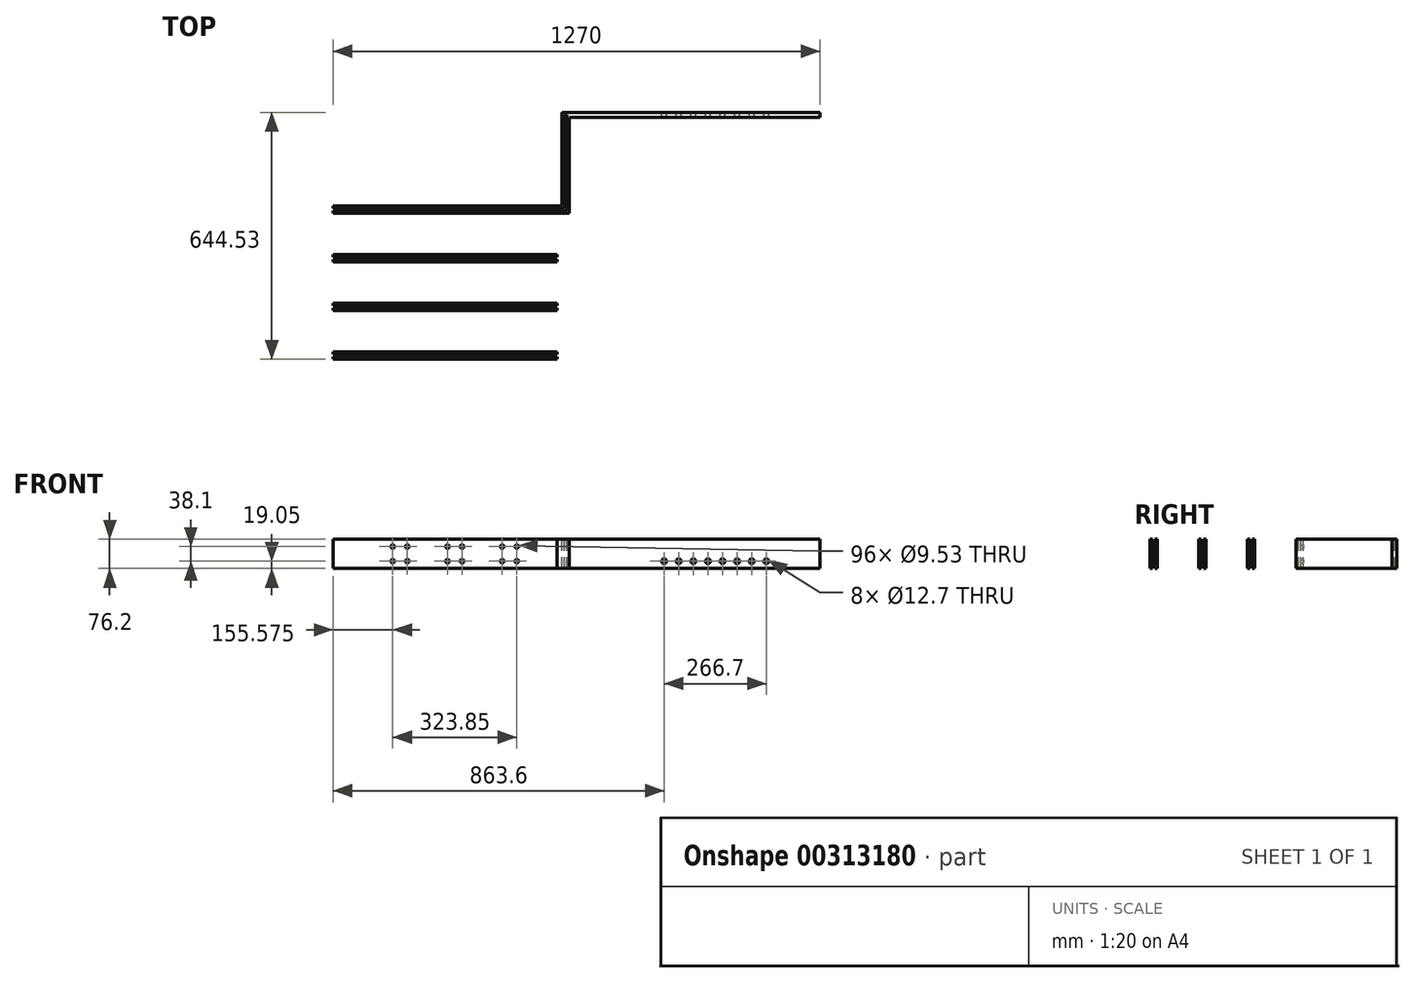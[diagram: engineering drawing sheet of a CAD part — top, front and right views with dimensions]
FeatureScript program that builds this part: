
annotation { "Feature Type Name" : "Feature", "Feature Type Description" : "" }
export const myFeature = defineFeature(function(context is Context, id is Id, definition is map)
    precondition{}
    {
        {
            var Q0;
            Q0=qCreatedBy(makeId("Right.planeOp"),FACE);
            var sketch = newSketch(context, id + "F0", { "sketchPlane" : qUnion([Q0])});
            skLineSegment(sketch, "E0.bottom", {"start": v(0, 0) * mm, "end": v(6.35, 0) * mm});
            skLineSegment(sketch, "E0.top", {"start": v(0, 76.2) * mm, "end": v(6.35, 76.2) * mm});
            skLineSegment(sketch, "E0.left", {"start": v(0, 0) * mm, "end": v(0, 76.2) * mm});
            skLineSegment(sketch, "E0.right", {"start": v(6.35, 0) * mm, "end": v(6.35, 76.2) * mm});
            skLineSegment(sketch, "E1.bottom", {"start": v(12.7, 0) * mm, "end": v(19.05, 0) * mm});
            skLineSegment(sketch, "E1.top", {"start": v(12.7, 76.2) * mm, "end": v(19.05, 76.2) * mm});
            skLineSegment(sketch, "E1.left", {"start": v(12.7, 0) * mm, "end": v(12.7, 76.2) * mm});
            skLineSegment(sketch, "E1.right", {"start": v(19.05, 0) * mm, "end": v(19.05, 76.2) * mm});
            skLineSegment(sketch, "E2.1.0.0", {"start": v(133.35, 0) * mm, "end": v(133.35, 76.2) * mm});
            skLineSegment(sketch, "E2.1.0.1", {"start": v(127, 0) * mm, "end": v(127, 76.2) * mm});
            skLineSegment(sketch, "E2.1.0.2", {"start": v(127, 76.2) * mm, "end": v(133.35, 76.2) * mm});
            skLineSegment(sketch, "E2.1.0.3", {"start": v(127, 0) * mm, "end": v(133.35, 0) * mm});
            skLineSegment(sketch, "E2.1.0.4", {"start": v(139.7, 0) * mm, "end": v(139.7, 76.2) * mm});
            skLineSegment(sketch, "E2.1.0.5", {"start": v(146.05, 0) * mm, "end": v(146.05, 76.2) * mm});
            skLineSegment(sketch, "E2.1.0.6", {"start": v(139.7, 76.2) * mm, "end": v(146.05, 76.2) * mm});
            skLineSegment(sketch, "E2.1.0.7", {"start": v(139.7, 0) * mm, "end": v(146.05, 0) * mm});
            skLineSegment(sketch, "E2.2.0.0", {"start": v(260.35, 0) * mm, "end": v(260.35, 76.2) * mm});
            skLineSegment(sketch, "E2.2.0.1", {"start": v(254, 0) * mm, "end": v(254, 76.2) * mm});
            skLineSegment(sketch, "E2.2.0.2", {"start": v(254, 76.2) * mm, "end": v(260.35, 76.2) * mm});
            skLineSegment(sketch, "E2.2.0.3", {"start": v(254, 0) * mm, "end": v(260.35, 0) * mm});
            skLineSegment(sketch, "E2.2.0.4", {"start": v(266.7, 0) * mm, "end": v(266.7, 76.2) * mm});
            skLineSegment(sketch, "E2.2.0.5", {"start": v(273.05, 0) * mm, "end": v(273.05, 76.2) * mm});
            skLineSegment(sketch, "E2.2.0.6", {"start": v(266.7, 76.2) * mm, "end": v(273.05, 76.2) * mm});
            skLineSegment(sketch, "E2.2.0.7", {"start": v(266.7, 0) * mm, "end": v(273.05, 0) * mm});
            skLineSegment(sketch, "E2.3.0.0", {"start": v(387.35, 0) * mm, "end": v(387.35, 76.2) * mm});
            skLineSegment(sketch, "E2.3.0.1", {"start": v(381, 0) * mm, "end": v(381, 76.2) * mm});
            skLineSegment(sketch, "E2.3.0.2", {"start": v(381, 76.2) * mm, "end": v(387.35, 76.2) * mm});
            skLineSegment(sketch, "E2.3.0.3", {"start": v(381, 0) * mm, "end": v(387.35, 0) * mm});
            skLineSegment(sketch, "E2.3.0.4", {"start": v(393.7, 0) * mm, "end": v(393.7, 76.2) * mm});
            skLineSegment(sketch, "E2.3.0.5", {"start": v(400.05, 0) * mm, "end": v(400.05, 76.2) * mm});
            skLineSegment(sketch, "E2.3.0.6", {"start": v(393.7, 76.2) * mm, "end": v(400.05, 76.2) * mm});
            skLineSegment(sketch, "E2.3.0.7", {"start": v(393.7, 0) * mm, "end": v(400.05, 0) * mm});
            skLineSegment(sketch, "E2.direction1", {"start": v(0, 0) * mm, "end": v(127, 0) * mm, "construction": true});
            skSolve(sketch);
        }
        {
            var Q0;
            Q0 = qSketchRegion(id + "F0", true);
            extrude(context, id + "F1", {"entities" : qUnion([Q0]), "depth" : 584.2 * mm});
        }
        {
            var Q0;
            Q0=makeQuery(id+"F1.opExtrude","SWEPT_FACE",FACE,{"disambiguationData":[OSD([sQuery(id+"F0.wireOp",EDGE,"E2.3.0.6")])]});
            var sketch = newSketch(context, id + "F2", { "sketchPlane" : qUnion([Q0])});
            skLineSegment(sketch, "E3", {"start": v(584.2, 393.7) * mm, "end": v(584.2, 400.05) * mm});
            skLineSegment(sketch, "E4", {"start": v(584.2, 400.05) * mm, "end": v(596.9, 400.05) * mm});
            skLineSegment(sketch, "E5", {"start": v(596.9, 400.05) * mm, "end": v(596.9, 644.53) * mm});
            skLineSegment(sketch, "E6", {"start": v(596.9, 644.53) * mm, "end": v(1270, 644.53) * mm});
            skLineSegment(sketch, "E7", {"start": v(1270, 644.53) * mm, "end": v(1270, 638.18) * mm});
            skLineSegment(sketch, "E8", {"start": v(1270, 638.18) * mm, "end": v(603.25, 638.18) * mm});
            skLineSegment(sketch, "E9", {"start": v(603.25, 638.18) * mm, "end": v(603.25, 393.7) * mm});
            skLineSegment(sketch, "E10", {"start": v(603.25, 393.7) * mm, "end": v(584.2, 393.7) * mm});
            skSolve(sketch);
        }
        {
            var Q0;
            Q0 = qSketchRegion(id + "F2", true);
            extrude(context, id + "F3", {"entities" : qUnion([Q0]), "operationType" : NewBodyOperationType.ADD, "oppositeDirection" : true, "depth" : 76.2 * mm});
        }
        {
            var Q0;
            Q0=makeQuery(id+"F1.opExtrude","SWEPT_FACE",FACE,{"disambiguationData":[OSD([sQuery(id+"F0.wireOp",EDGE,"E2.3.0.2")])]});
            var sketch = newSketch(context, id + "F4", { "sketchPlane" : qUnion([Q0])});
            skLineSegment(sketch, "E11", {"start": v(584.2, 387.35) * mm, "end": v(609.6, 387.35) * mm});
            skLineSegment(sketch, "E12", {"start": v(609.6, 387.35) * mm, "end": v(609.6, 638.18) * mm});
            skLineSegment(sketch, "E13", {"start": v(609.6, 638.18) * mm, "end": v(1270, 638.18) * mm});
            skLineSegment(sketch, "E14", {"start": v(1270, 638.18) * mm, "end": v(1270, 631.83) * mm});
            skLineSegment(sketch, "E15", {"start": v(1270, 631.83) * mm, "end": v(615.95, 631.82) * mm});
            skLineSegment(sketch, "E16", {"start": v(615.95, 631.82) * mm, "end": v(615.95, 381) * mm});
            skLineSegment(sketch, "E17", {"start": v(615.95, 381) * mm, "end": v(584.2, 381) * mm});
            skLineSegment(sketch, "E18", {"start": v(584.2, 381) * mm, "end": v(584.2, 387.35) * mm});
            skSolve(sketch);
        }
        {
            var Q0;
            Q0 = qSketchRegion(id + "F4", true);
            extrude(context, id + "F5", {"entities" : qUnion([Q0]), "operationType" : NewBodyOperationType.ADD, "oppositeDirection" : true, "depth" : 76.2 * mm});
        }
        {
            var Q0;
            Q0=makeQuery(id+"F3.opExtrude","SWEPT_FACE",FACE,{"disambiguationData":[OSD([sQuery(id+"F2.wireOp",EDGE,"E6")])]});
            var sketch = newSketch(context, id + "F6", { "sketchPlane" : qUnion([Q0])});
            skCircle(sketch, "E19", {"center": v(-1130.3, 19.05) * mm, "radius": 6.35 * mm});
            skCircle(sketch, "E20.1.0.0", {"center": v(-1092.2, 19.05) * mm, "radius": 6.35 * mm});
            skCircle(sketch, "E20.2.0.0", {"center": v(-1054.1, 19.05) * mm, "radius": 6.35 * mm});
            skCircle(sketch, "E20.3.0.0", {"center": v(-1016, 19.05) * mm, "radius": 6.35 * mm});
            skLineSegment(sketch, "E20.direction1", {"start": v(-1130.3, 19.05) * mm, "end": v(-1092.2, 19.05) * mm, "construction": true});
            skCircle(sketch, "E21.0.4.0", {"center": v(-977.9, 19.05) * mm, "radius": 6.35 * mm});
            skCircle(sketch, "E21.0.5.0", {"center": v(-939.8, 19.05) * mm, "radius": 6.35 * mm});
            skCircle(sketch, "E21.0.6.0", {"center": v(-901.7, 19.05) * mm, "radius": 6.35 * mm});
            skCircle(sketch, "E21.0.7.0", {"center": v(-863.6, 19.05) * mm, "radius": 6.35 * mm});
            skLineSegment(sketch, "E22", {"start": v(-1130.3, 19.05) * mm, "end": v(-863.6, 19.05) * mm, "construction": true});
            skPoint(sketch, "E23", {"position": v(-996.95, 19.05) * mm});
            skSolve(sketch);
        }
        {
            var Q0;
            Q0 = qSketchRegion(id + "F6", true);
            extrude(context, id + "F7", {"entities" : qUnion([Q0]), "operationType" : NewBodyOperationType.REMOVE, "endBound" : BoundingType.THROUGH_ALL, "oppositeDirection" : true, "depth" : 25.4 * mm});
        }
        {
            var Q0;
            Q0=makeQuery(id+"F3.boolean.opBoolean","MERGE",FACE,{"derivedFrom":[makeQuery(id+"F1.opExtrude","SWEPT_FACE",FACE,{"disambiguationData":[OSD([sQuery(id+"F0.wireOp",EDGE,"E2.3.0.5")])]}),makeQuery(id+"F3.opExtrude","SWEPT_FACE",FACE,{"disambiguationData":[OSD([sQuery(id+"F2.wireOp",EDGE,"E4")])]})]});
            var sketch = newSketch(context, id + "F8", { "sketchPlane" : qUnion([Q0])});
            skLineSegment(sketch, "E24.bottom", {"start": v(-298.45, 57.15) * mm, "end": v(-336.55, 57.15) * mm, "construction": true});
            skLineSegment(sketch, "E24.top", {"start": v(-298.45, 19.05) * mm, "end": v(-336.55, 19.05) * mm, "construction": true});
            skLineSegment(sketch, "E24.left", {"start": v(-298.45, 57.15) * mm, "end": v(-298.45, 19.05) * mm, "construction": true});
            skLineSegment(sketch, "E24.right", {"start": v(-336.55, 57.15) * mm, "end": v(-336.55, 19.05) * mm, "construction": true});
            skPoint(sketch, "E24.middle", {"position": v(-317.5, 38.1) * mm});
            skPoint(sketch, "E24.middle.positionSnap0", {"position": v(0, 38.1) * mm});
            skPoint(sketch, "E24.centerSnap0", {"position": v(0, 38.1) * mm});
            skCircle(sketch, "E25", {"center": v(-298.45, 57.15) * mm, "radius": 4.76 * mm});
            skCircle(sketch, "E26", {"center": v(-298.45, 19.05) * mm, "radius": 4.76 * mm});
            skCircle(sketch, "E27", {"center": v(-336.55, 19.05) * mm, "radius": 4.76 * mm});
            skCircle(sketch, "E28", {"center": v(-336.55, 57.15) * mm, "radius": 4.76 * mm});
            skLineSegment(sketch, "E29.bottom", {"start": v(-155.57, 57.15) * mm, "end": v(-193.67, 57.15) * mm, "construction": true});
            skLineSegment(sketch, "E29.top", {"start": v(-155.57, 19.05) * mm, "end": v(-193.67, 19.05) * mm, "construction": true});
            skLineSegment(sketch, "E29.left", {"start": v(-155.57, 57.15) * mm, "end": v(-155.57, 19.05) * mm, "construction": true});
            skLineSegment(sketch, "E29.right", {"start": v(-193.67, 57.15) * mm, "end": v(-193.67, 19.05) * mm, "construction": true});
            skPoint(sketch, "E29.middle", {"position": v(-174.62, 38.1) * mm});
            skCircle(sketch, "E30", {"center": v(-155.57, 57.15) * mm, "radius": 4.76 * mm});
            skCircle(sketch, "E31", {"center": v(-155.57, 19.05) * mm, "radius": 4.76 * mm});
            skCircle(sketch, "E32", {"center": v(-193.67, 19.05) * mm, "radius": 4.76 * mm});
            skCircle(sketch, "E33", {"center": v(-193.67, 57.15) * mm, "radius": 4.76 * mm});
            skLineSegment(sketch, "E34.bottom", {"start": v(-441.32, 57.15) * mm, "end": v(-479.43, 57.15) * mm, "construction": true});
            skLineSegment(sketch, "E34.top", {"start": v(-441.32, 19.05) * mm, "end": v(-479.43, 19.05) * mm, "construction": true});
            skLineSegment(sketch, "E34.left", {"start": v(-441.32, 57.15) * mm, "end": v(-441.32, 19.05) * mm, "construction": true});
            skLineSegment(sketch, "E34.right", {"start": v(-479.43, 57.15) * mm, "end": v(-479.43, 19.05) * mm, "construction": true});
            skPoint(sketch, "E34.middle", {"position": v(-460.38, 38.1) * mm});
            skCircle(sketch, "E35", {"center": v(-441.32, 57.15) * mm, "radius": 4.76 * mm});
            skCircle(sketch, "E36", {"center": v(-441.32, 19.05) * mm, "radius": 4.76 * mm});
            skCircle(sketch, "E37", {"center": v(-479.43, 19.05) * mm, "radius": 4.76 * mm});
            skCircle(sketch, "E38", {"center": v(-479.43, 57.15) * mm, "radius": 4.76 * mm});
            skSolve(sketch);
        }
        {
            var Q0;
            Q0 = qSketchRegion(id + "F8", true);
            extrude(context, id + "F9", {"entities" : qUnion([Q0]), "operationType" : NewBodyOperationType.REMOVE, "endBound" : BoundingType.THROUGH_ALL, "oppositeDirection" : true, "depth" : 25.4 * mm});
        }
    });
